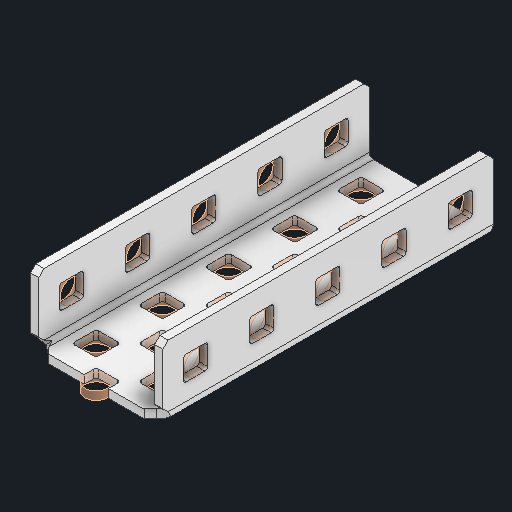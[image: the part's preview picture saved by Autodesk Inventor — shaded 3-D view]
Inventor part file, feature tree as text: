
AUTODESK INVENTOR PART (.ipt)
format: ipt  version: 2024 (Build 280153000, 153)  size: 571,904 bytes
history: native  units: in
note: dims shown in document units (in); Inventor stores cm internally (conversion verified against a paired STEP export)
features: other x56, sketch x5, sheet_metal_op x1
ambient origin geometry x8: Origin, YZ Plane, XZ Plane, XY Plane, X Axis, Y Axis, Z Axis, Center Point
bodies: Solid1 (feature_tree)
feature tree (62):
  other  "Alu C 1x2x1x5.ipt"
  other  "Solid1::Alu C 1x2x1x5.ipt"
  other  "TaggingFeature1"
  sketch  "Sketch1"  dims[d0=0.3937in]
  sketch  "Sketch2"  dims[d1=0.0625in]
  sketch  "Sketch3"
  other  "Flange Pattern Sketch"
  sketch  "Sketch9"
  sheet_metal_op  "Body Pattern Sketch"
  other  "Arc Length"
  sketch  "Sketch14"
  other  "Flange Pattern Plane"
  other  "Srf1"
  other  "Srf2"
  other  "Srf3"
  other  "Srf4"
  other  "Srf5"
  other  "Srf6"
  other  "Srf7"
  other  "Srf8"
  other  "Srf9"
  other  "Srf10"
  other  "Srf11"
  other  "Srf12"
  other  "Srf13"
  other  "Srf14"
  other  "Srf15"
  other  "Srf16"
  other  "Srf17"
  other  "Srf18"
  other  "Srf19"
  other  "Srf20"
  other  "Srf21"
  other  "Srf22"
  other  "Srf23"
  other  "Srf24"
  other  "Srf25"
  other  "Srf1::Derived"
  other  "Srf2::Derived"
  other  "Srf823::Derived"
  other  "Srf824::Derived"
  other  "Srf825::Derived"
  other  "Srf826::Derived"
  other  "Srf827::Derived"
  other  "Srf828::Derived"
  other  "Srf829::Derived"
  other  "Srf922::Derived"
  other  "Srf91::Derived"
  other  "Srf92::Derived"
  other  "Srf856::Derived"
  other  "Srf857::Derived"
  other  "Srf858::Derived"
  other  "Srf859::Derived"
  other  "Srf860::Derived"
  other  "Srf861::Derived"
  other  "Srf862::Derived"
  other  "Srf959::Derived"
  other  "Srf786::Derived"
  other  "Srf889::Derived"
  other  "Srf890::Derived"
  other  "Srf891::Derived"
  other  "Srf892::Derived"
